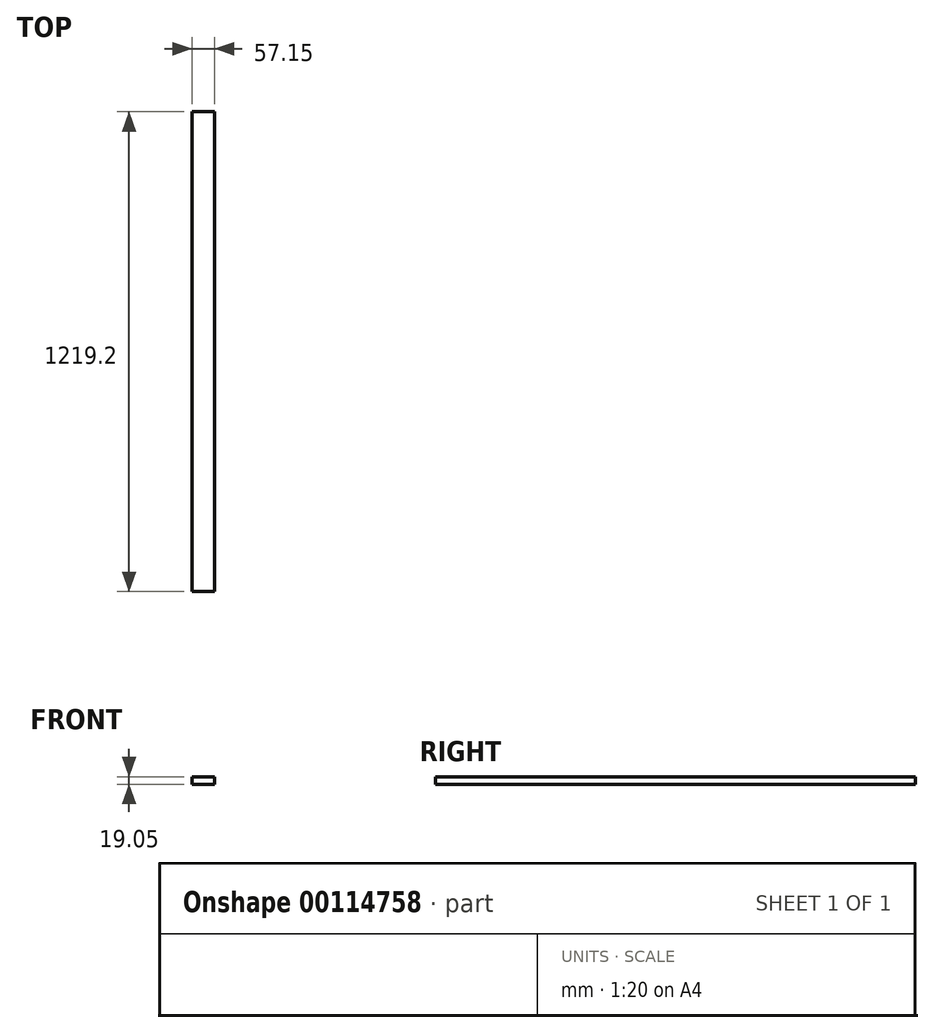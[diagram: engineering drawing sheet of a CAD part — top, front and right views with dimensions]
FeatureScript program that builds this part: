
annotation { "Feature Type Name" : "Feature", "Feature Type Description" : "" }
export const myFeature = defineFeature(function(context is Context, id is Id, definition is map)
    precondition{}
    {
        {
            var Q0;
            Q0=qCreatedBy(makeId("Top.planeOp"),FACE);
            var sketch = newSketch(context, id + "F0", { "sketchPlane" : qUnion([Q0])});
            skLineSegment(sketch, "E0.bottom", {"start": v(0, 0) * mm, "end": v(57.15, 0) * mm});
            skLineSegment(sketch, "E0.top", {"start": v(0, 1219.2) * mm, "end": v(57.15, 1219.2) * mm});
            skLineSegment(sketch, "E0.left", {"start": v(0, 0) * mm, "end": v(0, 1219.2) * mm});
            skLineSegment(sketch, "E0.right", {"start": v(57.15, 0) * mm, "end": v(57.15, 1219.2) * mm});
            skSolve(sketch);
        }
        {
            var Q0;
            Q0=qSketchRegion(id+"F0",true);
            extrude(context, id + "F1", {"entities" : qUnion([Q0]), "depth" : 19.05 * mm});
        }
    });
